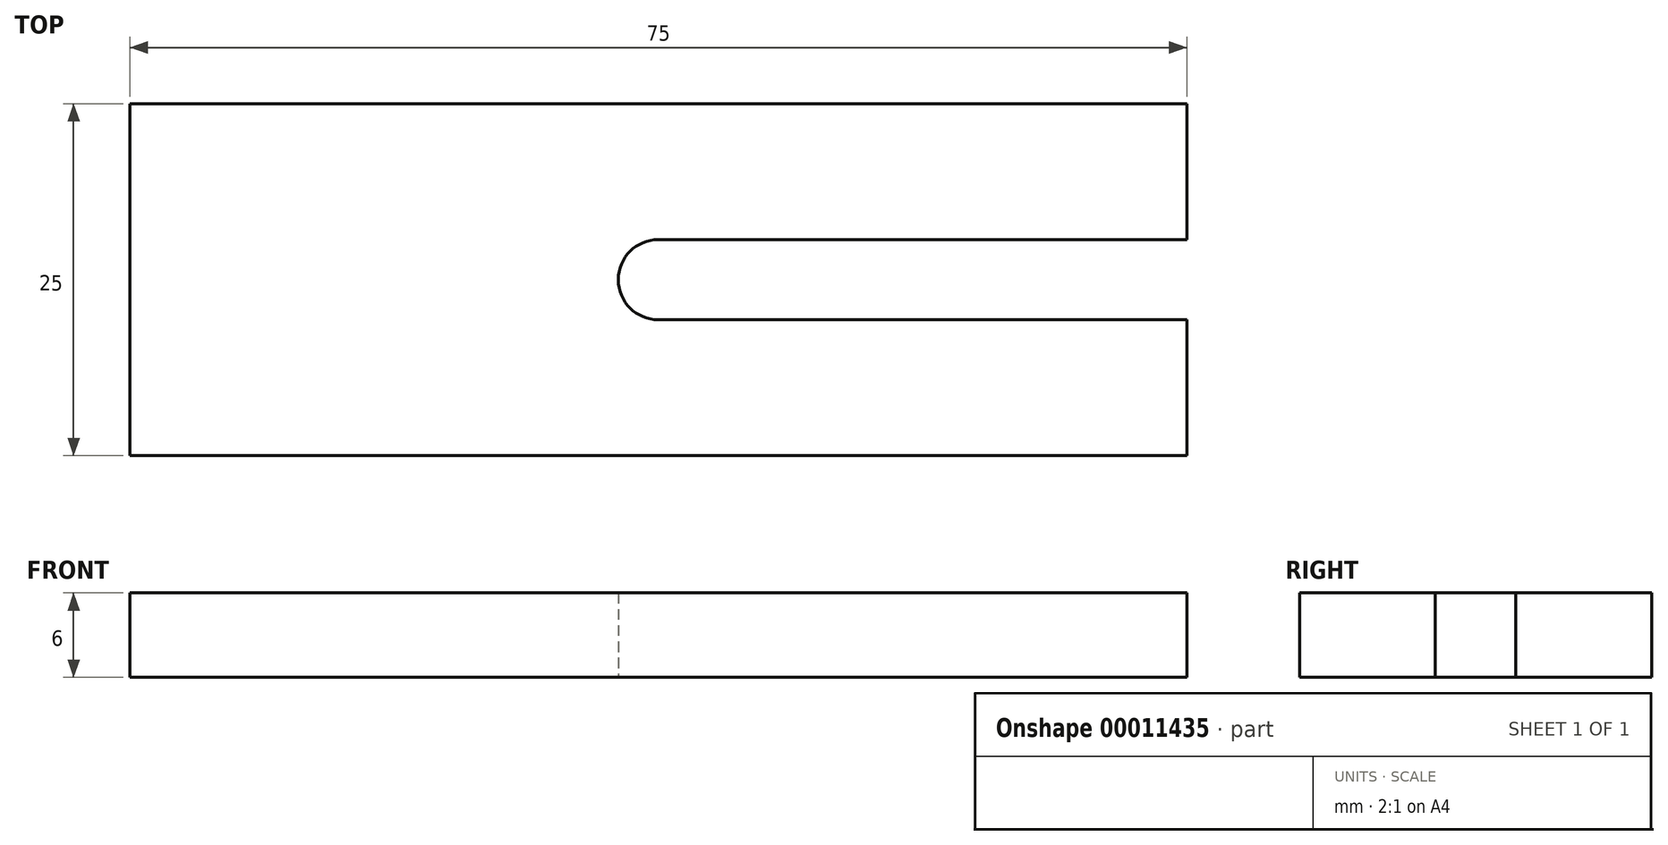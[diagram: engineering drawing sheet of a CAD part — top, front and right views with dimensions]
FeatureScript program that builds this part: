
annotation { "Feature Type Name" : "Feature", "Feature Type Description" : "" }
export const myFeature = defineFeature(function(context is Context, id is Id, definition is map)
    precondition{}
    {
        {
            var Q0;
            Q0=qCreatedBy(makeId("Top.planeOp"),FACE);
            var sketch = newSketch(context, id + "F0", { "sketchPlane" : qUnion([Q0])});
            skLineSegment(sketch, "E0.bottom", {"start": v(-37.5, 12.5) * mm, "end": v(37.5, 12.5) * mm});
            skLineSegment(sketch, "E0.top", {"start": v(-37.5, -12.5) * mm, "end": v(37.5, -12.5) * mm});
            skLineSegment(sketch, "E0.left", {"start": v(-37.5, 12.5) * mm, "end": v(-37.5, -12.5) * mm});
            skLineSegment(sketch, "E0.right", {"start": v(37.5, 12.5) * mm, "end": v(37.5, 2.85) * mm});
            skLineSegment(sketch, "E1", {"start": v(37.5, 2.85) * mm, "end": v(0, 2.85) * mm});
            skLineSegment(sketch, "E2", {"start": v(37.5, -2.85) * mm, "end": v(0, -2.85) * mm});
            skArc(sketch, "E3", {"start": v(0, 2.85) * mm, "mid": v(-2.85, 0) * mm, "end": v(0, -2.85) * mm});
            skLineSegment(sketch, "E4.trimOffspring", {"start": v(37.5, -2.85) * mm, "end": v(37.5, -12.5) * mm});
            skSolve(sketch);
        }
        {
            var Q0;
            Q0=makeQuery(id+"F0.imprint","IMPRINT",FACE,{"disambiguationData":[TD([[makeQuery(id+"F0.imprint","IMPRINT",EDGE,{"derivedFrom":sQuery(id+"F0.wireOp",EDGE,"E0.bottom")}),-1.0]])]});
            extrude(context, id + "F1", {"entities" : qUnion([Q0]), "endBound" : BoundingType.SYMMETRIC, "depth" : 6 * mm});
        }
    });
